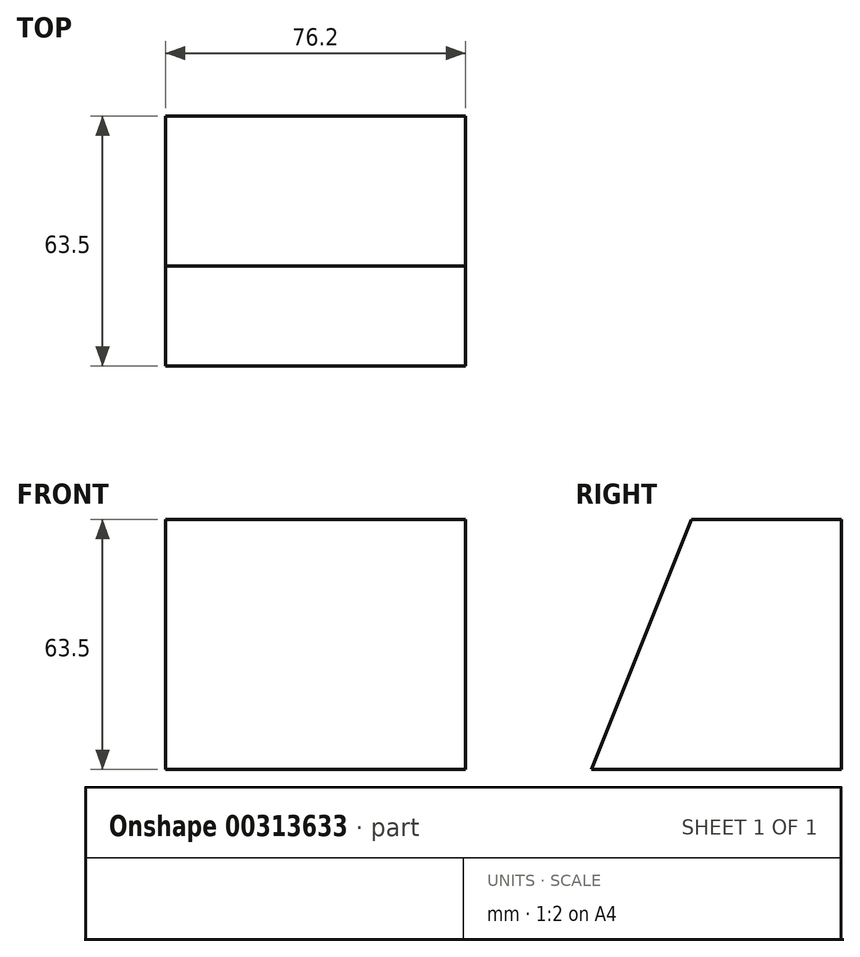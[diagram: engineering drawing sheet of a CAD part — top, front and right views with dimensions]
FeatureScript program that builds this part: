
annotation { "Feature Type Name" : "Feature", "Feature Type Description" : "" }
export const myFeature = defineFeature(function(context is Context, id is Id, definition is map)
    precondition{}
    {
        {
            var Q0;
            Q0=qCreatedBy(makeId("Right.planeOp"),FACE);
            var sketch = newSketch(context, id + "F0", { "sketchPlane" : qUnion([Q0])});
            skLineSegment(sketch, "E0", {"start": v(-19.53, -54.65) * mm, "end": v(43.97, -54.65) * mm});
            skLineSegment(sketch, "E1", {"start": v(43.97, -54.65) * mm, "end": v(43.97, 8.85) * mm});
            skLineSegment(sketch, "E2", {"start": v(43.97, 8.85) * mm, "end": v(5.87, 8.85) * mm});
            skLineSegment(sketch, "E3", {"start": v(5.87, 8.85) * mm, "end": v(-19.53, -54.65) * mm});
            skSolve(sketch);
        }
        {
            var Q0;
            Q0 = qSketchRegion(id + "F0", true);
            extrude(context, id + "F1", {"entities" : qUnion([Q0]), "depth" : 76.2 * mm});
        }
    });
